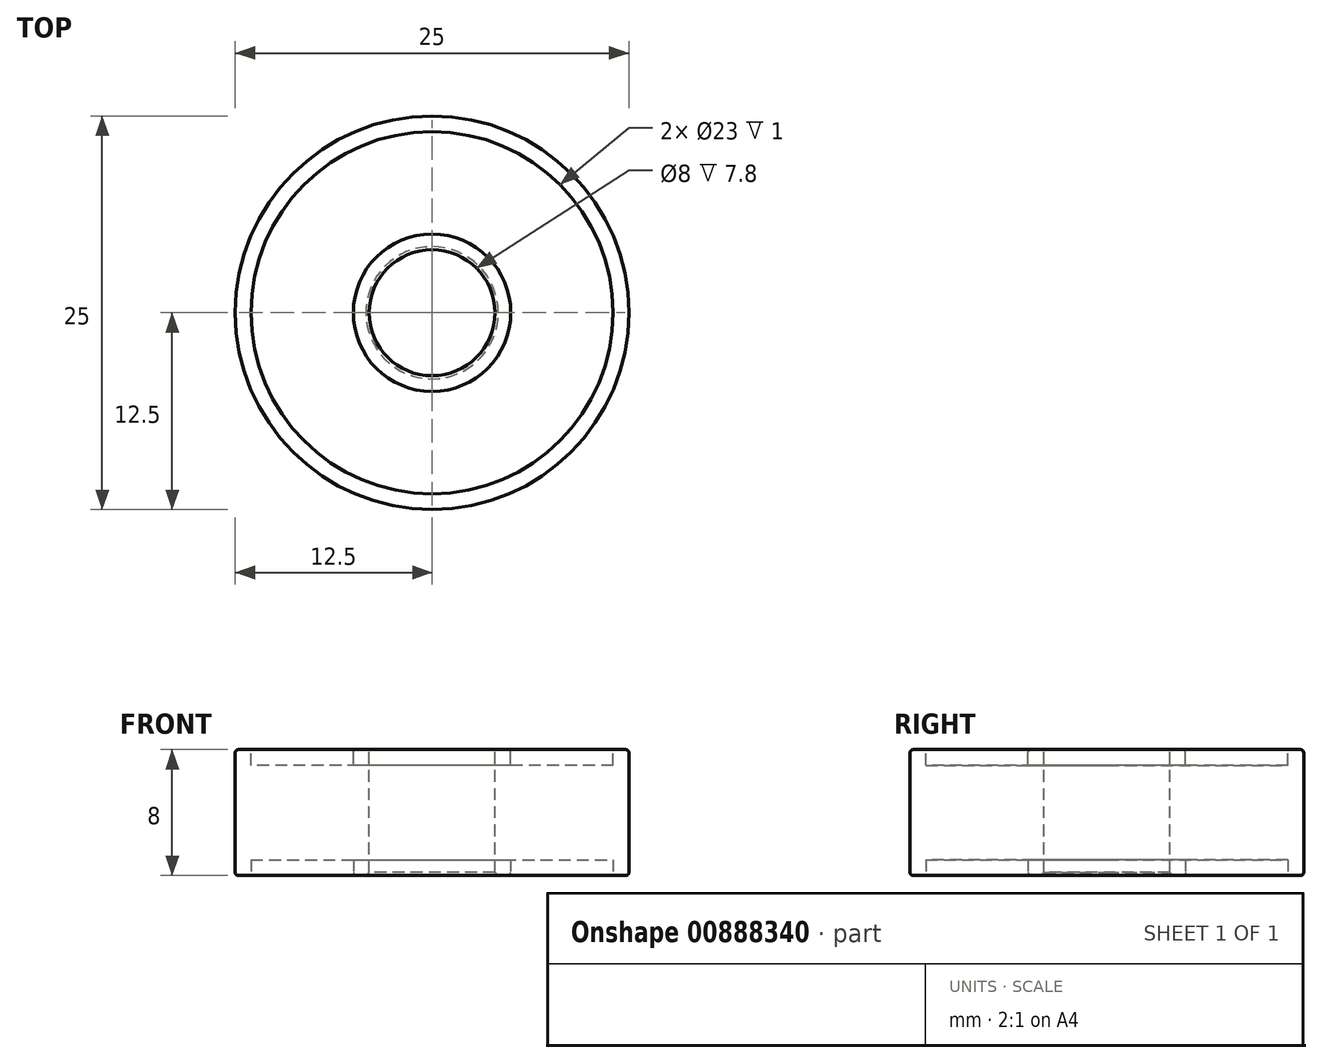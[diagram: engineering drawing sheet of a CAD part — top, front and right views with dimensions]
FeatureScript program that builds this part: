
annotation { "Feature Type Name" : "Feature", "Feature Type Description" : "" }
export const myFeature = defineFeature(function(context is Context, id is Id, definition is map)
    precondition{}
    {
        {
            var Q0;
            Q0=qCreatedBy(makeId("Top.planeOp"),FACE);
            var sketch = newSketch(context, id + "F0", { "sketchPlane" : qUnion([Q0])});
            skCircle(sketch, "E0", {"center": v(0, 0) * mm, "radius": 12.5 * mm});
            skSolve(sketch);
        }
        {
            var Q0;
            Q0=makeQuery(id+"F0.imprint","IMPRINT",FACE,{"disambiguationData":[TD([[makeQuery(id+"F0.imprint","IMPRINT",EDGE,{"derivedFrom":sQuery(id+"F0.wireOp",EDGE,"E0")}),1.0]])]});
            extrude(context, id + "F1", {"entities" : qUnion([Q0]), "depth" : 8 * mm, "offsetDistance" : 25.4 * mm});
        }
        {
            var Q0;
            Q0=makeQuery(id+"F1.opExtrude","CAP_FACE",FACE,{"disambiguationData":[OSD([sQuery(id+"F0.wireOp",EDGE,"E0")])],"isStart":false});
            var sketch = newSketch(context, id + "F2", { "sketchPlane" : qUnion([Q0])});
            skCircle(sketch, "E1", {"center": v(0, 0) * mm, "radius": 5 * mm});
            skCircle(sketch, "E2", {"center": v(0, 0) * mm, "radius": 11.5 * mm});
            skCircle(sketch, "E3", {"center": v(0, 0) * mm, "radius": 4 * mm});
            skSolve(sketch);
        }
        {
            var Q0;
            Q0=makeQuery(id+"F2.imprint","IMPRINT",FACE,{"disambiguationData":[TD([[makeQuery(id+"F2.imprint","IMPRINT",EDGE,{"derivedFrom":sQuery(id+"F2.wireOp",EDGE,"E3")}),1.0]])]});
            extrude(context, id + "F3", {"entities" : qUnion([Q0]), "operationType" : NewBodyOperationType.REMOVE, "endBound" : BoundingType.THROUGH_ALL, "oppositeDirection" : true, "depth" : 25.4 * mm, "offsetDistance" : 25.4 * mm});
        }
        {
            var Q0;
            Q0 = qSketchRegion(id + "F2", true);
            extrude(context, id + "F4", {"entities" : qUnion([Q0]), "operationType" : NewBodyOperationType.REMOVE, "oppositeDirection" : true, "depth" : 1 * mm, "offsetDistance" : 25.4 * mm});
        }
        {
            var Q0;
            Q0=makeQuery(id+"F1.opExtrude","CAP_FACE",FACE,{"disambiguationData":[OSD([sQuery(id+"F0.wireOp",EDGE,"E0")])],"isStart":true});
            var sketch = newSketch(context, id + "F5", { "sketchPlane" : qUnion([Q0])});
            skCircle(sketch, "E4", {"center": v(0, 0) * mm, "radius": 5 * mm});
            skCircle(sketch, "E5", {"center": v(0, 0) * mm, "radius": 11.5 * mm});
            skSolve(sketch);
        }
        {
            var Q0;
            Q0=makeQuery(id+"F5.imprint","IMPRINT",FACE,{"disambiguationData":[TD([[makeQuery(id+"F5.imprint","IMPRINT",EDGE,{"derivedFrom":sQuery(id+"F5.wireOp",EDGE,"E4")}),-1.0]])]});
            extrude(context, id + "F6", {"entities" : qUnion([Q0]), "operationType" : NewBodyOperationType.REMOVE, "oppositeDirection" : true, "depth" : 1 * mm, "offsetDistance" : 25.4 * mm});
        }
        {
            var Q0;
            Q0=makeQuery(id+"F1.opExtrude","CAP_EDGE",EDGE,{"disambiguationData":[OSD([sQuery(id+"F0.wireOp",EDGE,"E0")])],"isStart":false});
            var Q1;
            Q1=makeQuery(id+"F1.opExtrude","CAP_EDGE",EDGE,{"disambiguationData":[OSD([sQuery(id+"F0.wireOp",EDGE,"E0")])],"isStart":true});
            var Q2;
            Q2=makeQuery(id+"F4.boolean.opBoolean","COPY",EDGE,{"derivedFrom":makeQuery(id+"F4.opExtrude","CAP_EDGE",EDGE,{"disambiguationData":[OSD([sQuery(id+"F2.wireOp",EDGE,"E1")])],"isStart":true})});
            var Q3;
            Q3=makeQuery(id+"F6.boolean.opBoolean","COPY",EDGE,{"derivedFrom":makeQuery(id+"F6.opExtrude","CAP_EDGE",EDGE,{"disambiguationData":[OSD([sQuery(id+"F5.wireOp",EDGE,"E4")])],"isStart":true})});
            fillet(context, id + "F7", {"entities" : qUnion([Q0, Q1, Q2, Q3]), "radius" : 0.2 * mm, "tangentPropagation" : true, "allowEdgeOverflow" : false});
        }
        {
            var Q0;
            Q0=makeQuery(id+"F3.boolean.opBoolean","COPY",EDGE,{"derivedFrom":makeQuery(id+"F3.opExtrude","CAP_EDGE",EDGE,{"disambiguationData":[OSD([sQuery(id+"F2.wireOp",EDGE,"E3")])],"isStart":true})});
            var Q1;
            Q1=makeQuery(id+"F3.boolean.opBoolean","INTERSECT",EDGE,{"derivedFrom":[makeQuery(id+"F1.opExtrude","CAP_FACE",FACE,{"disambiguationData":[OSD([sQuery(id+"F0.wireOp",EDGE,"E0")])],"isStart":true}),makeQuery(id+"F3.opExtrude","SWEPT_FACE",FACE,{"disambiguationData":[OSD([sQuery(id+"F2.wireOp",EDGE,"E3")])]})]});
            chamfer(context, id + "F8", {"entities" : qUnion([Q0, Q1]), "width" : .2 * mm, "tangentPropagation" : true});
        }
    });
